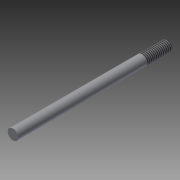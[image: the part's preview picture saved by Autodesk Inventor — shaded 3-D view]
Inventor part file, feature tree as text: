
AUTODESK INVENTOR PART (.ipt)
format: ipt  version: 2015 (Build 190159000, 159)  size: 70,656 bytes
history: native  units: mm
features: extrude x1, thread x1, sketch x1
ambient origin geometry x8: Origin, YZ Plane, XZ Plane, XY Plane, X Axis, Y Axis, Z Axis, Center Point
bodies: Solid1 (feature_tree)
feature tree (3):
  extrude  "Extrusion1"  Depth=89.0mm TaperAngle=0.0deg
  thread  "Thread1"  [1 undecoded]
  sketch  "Sketch1"  dims[d0=6.0mm d1=89.0mm d2=0.0mm d3=14.5mm d4=0.0mm]
note: 1 required parameter value undecoded (feature->parameter linkage not recoverable at this tier; creation-order binding heuristic only, values carry confidence <= 0.55)
